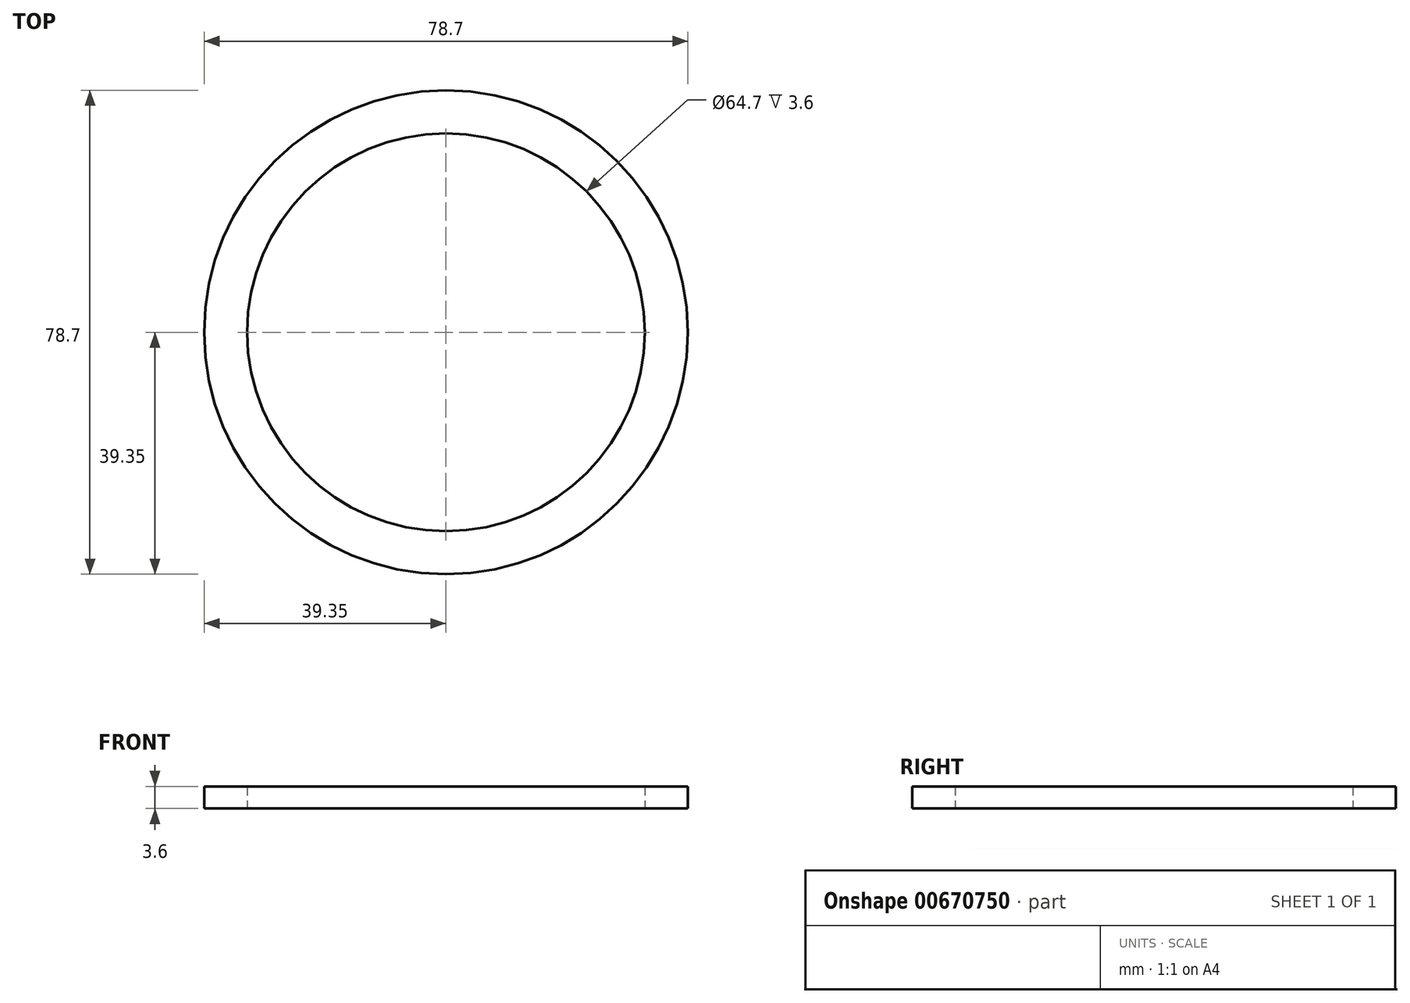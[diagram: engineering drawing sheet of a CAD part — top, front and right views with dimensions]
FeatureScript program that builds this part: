
annotation { "Feature Type Name" : "Feature", "Feature Type Description" : "" }
export const myFeature = defineFeature(function(context is Context, id is Id, definition is map)
    precondition{}
    {
        {
            var Q0;
            Q0=qCreatedBy(makeId("Front.planeOp"),FACE);
            var sketch = newSketch(context, id + "F0", { "sketchPlane" : qUnion([Q0])});
            skLineSegment(sketch, "E0.bottom", {"start": v(32.35, 0) * mm, "end": v(39.35, 0) * mm});
            skLineSegment(sketch, "E0.top", {"start": v(32.35, 3.6) * mm, "end": v(39.35, 3.6) * mm});
            skLineSegment(sketch, "E0.left", {"start": v(32.35, 0) * mm, "end": v(32.35, 3.6) * mm});
            skLineSegment(sketch, "E0.right", {"start": v(39.35, 0) * mm, "end": v(39.35, 3.6) * mm});
            skLineSegment(sketch, "E1", {"start": v(0, 0) * mm, "end": v(0, 11.67) * mm, "construction": true});
            skSolve(sketch);
        }
        {
            var Q0;
            Q0=makeQuery(id+"F0.imprint","IMPRINT",FACE,{"disambiguationData":[TD([[makeQuery(id+"F0.imprint","IMPRINT",EDGE,{"derivedFrom":sQuery(id+"F0.wireOp",EDGE,"E0.bottom")}),1.0]])]});
            var Q1;
            Q1=sQuery(id+"F0.wireOp",EDGE,"E1");
            revolve(context, id + "F1", {"entities" : qUnion([Q0]), "axis" : qUnion([Q1]), "revolveType" : RevolveType.FULL});
        }
    });
